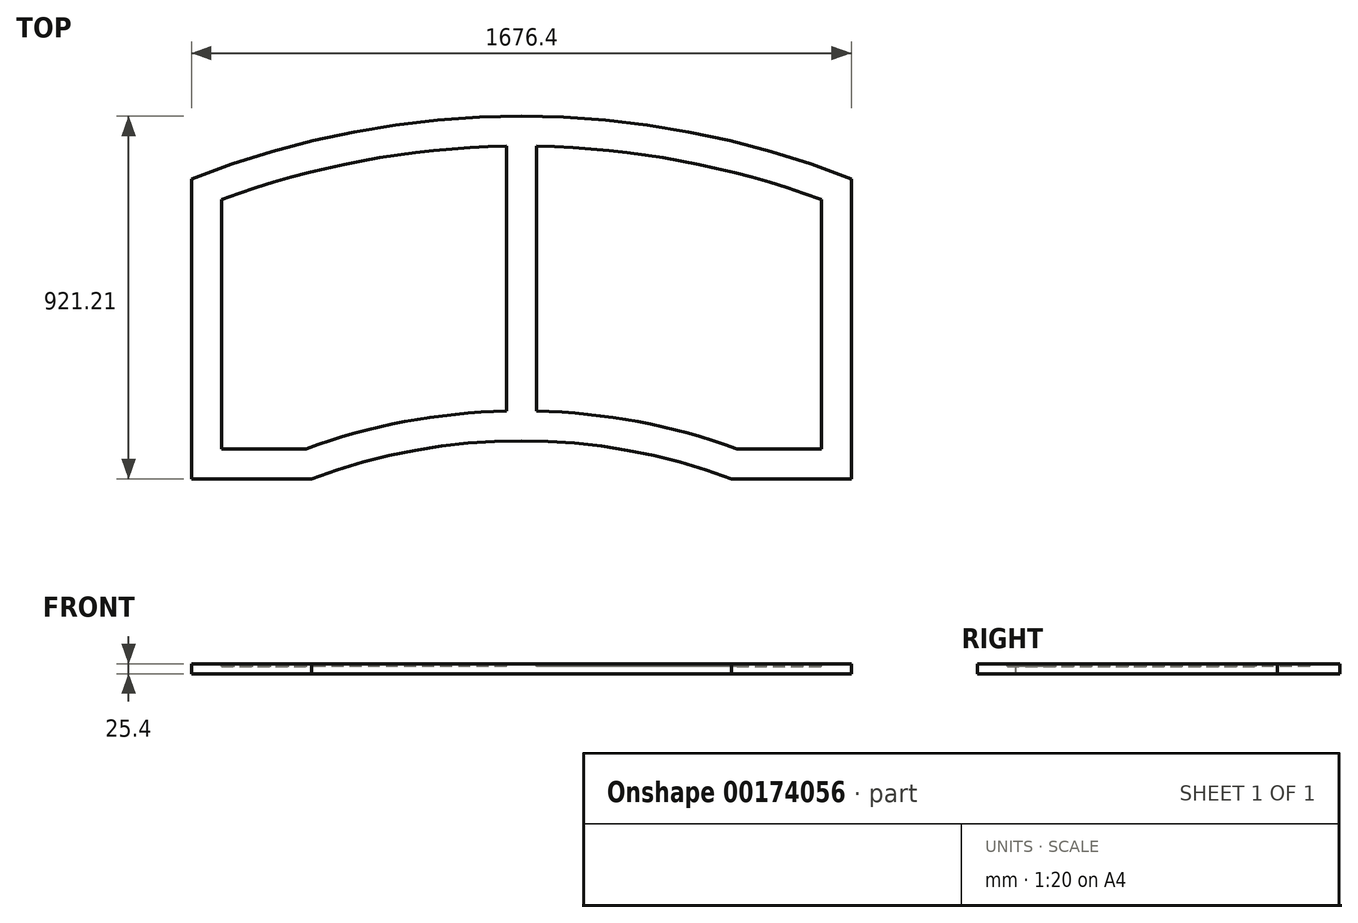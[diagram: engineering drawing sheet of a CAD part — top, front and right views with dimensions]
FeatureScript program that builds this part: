
annotation { "Feature Type Name" : "Feature", "Feature Type Description" : "" }
export const myFeature = defineFeature(function(context is Context, id is Id, definition is map)
    precondition{}
    {
        {
            var Q0;
            Q0=qCreatedBy(makeId("Top.planeOp"),FACE);
            var sketch = newSketch(context, id + "F0", { "sketchPlane" : qUnion([Q0])});
            skLineSegment(sketch, "E0.bottom", {"start": v(0, 0) * mm, "end": v(304.8, 0) * mm});
            skLineSegment(sketch, "E0.left", {"start": v(0, 0) * mm, "end": v(0, 762) * mm});
            skLineSegment(sketch, "E0.right", {"start": v(1676.4, 0) * mm, "end": v(1676.4, 762) * mm});
            skLineSegment(sketch, "E1.trimOffspring", {"start": v(1371.6, 0) * mm, "end": v(1676.4, 0) * mm});
            skArc(sketch, "E2", {"start": v(1676.4, 762) * mm, "mid": v(838.2, 921.21) * mm, "end": v(0, 762) * mm});
            skArc(sketch, "E3", {"start": v(1371.6, 0) * mm, "mid": v(838.2, 96.4) * mm, "end": v(304.8, 0) * mm});
            skLineSegment(sketch, "E4", {"start": v(838.2, -1427.6) * mm, "end": v(838.2, 2052.5) * mm, "construction": true});
            skSolve(sketch);
        }
        {
            var Q0;
            Q0=makeQuery(id+"F0.imprint","IMPRINT",FACE,{"disambiguationData":[TD([[makeQuery(id+"F0.imprint","IMPRINT",EDGE,{"derivedFrom":sQuery(id+"F0.wireOp",EDGE,"E0.bottom")}),1.0]])]});
            extrude(context, id + "F1", {"entities" : qUnion([Q0]), "depth" : 25.4 * mm});
        }
        {
            var Q0;
            Q0=makeQuery(id+"F1.opExtrude","CAP_FACE",FACE,{"disambiguationData":[OSD([sQuery(id+"F0.wireOp",EDGE,"E0.bottom"),sQuery(id+"F0.wireOp",EDGE,"E0.left"),sQuery(id+"F0.wireOp",EDGE,"E0.right"),sQuery(id+"F0.wireOp",EDGE,"E1.trimOffspring"),sQuery(id+"F0.wireOp",EDGE,"E2"),sQuery(id+"F0.wireOp",EDGE,"E3")])],"isStart":false});
            var sketch = newSketch(context, id + "F2", { "sketchPlane" : qUnion([Q0])});
            skLineSegment(sketch, "E5.0", {"start": v(1600.2, 76.2) * mm, "end": v(1600.2, 709.48) * mm});
            skLineSegment(sketch, "E5.1", {"start": v(76.2, 76.2) * mm, "end": v(76.2, 709.48) * mm});
            skLineSegment(sketch, "E5.2", {"start": v(76.2, 76.2) * mm, "end": v(291.2, 76.2) * mm});
            skArc(sketch, "E5.3", {"start": v(1600.2, 709.48) * mm, "mid": v(1243.92, 807.45) * mm, "end": v(876.3, 844.69) * mm});
            skArc(sketch, "E5.4", {"start": v(1385.2, 76.2) * mm, "mid": v(1134.66, 144.9) * mm, "end": v(876.3, 172.14) * mm});
            skLineSegment(sketch, "E5.5", {"start": v(1385.2, 76.2) * mm, "end": v(1600.2, 76.2) * mm});
            skLineSegment(sketch, "E6", {"start": v(838.2, 935.24) * mm, "end": v(838.2, 11.5) * mm, "construction": true});
            skLineSegment(sketch, "E7", {"start": v(800.1, 844.69) * mm, "end": v(800.1, 172.14) * mm});
            skLineSegment(sketch, "E8", {"start": v(876.3, 172.14) * mm, "end": v(876.3, 844.69) * mm});
            skArc(sketch, "E9.trimOffspring", {"start": v(800.1, 844.69) * mm, "mid": v(432.48, 807.45) * mm, "end": v(76.2, 709.48) * mm});
            skArc(sketch, "E10.trimOffspring", {"start": v(800.1, 172.14) * mm, "mid": v(541.74, 144.9) * mm, "end": v(291.2, 76.2) * mm});
            skSolve(sketch);
        }
        {
            var Q0;
            Q0 = qSketchRegion(id + "F2", true);
            extrude(context, id + "F3", {"entities" : qUnion([Q0]), "operationType" : NewBodyOperationType.REMOVE, "oppositeDirection" : true, "depth" : 6.35 * mm});
        }
    });
